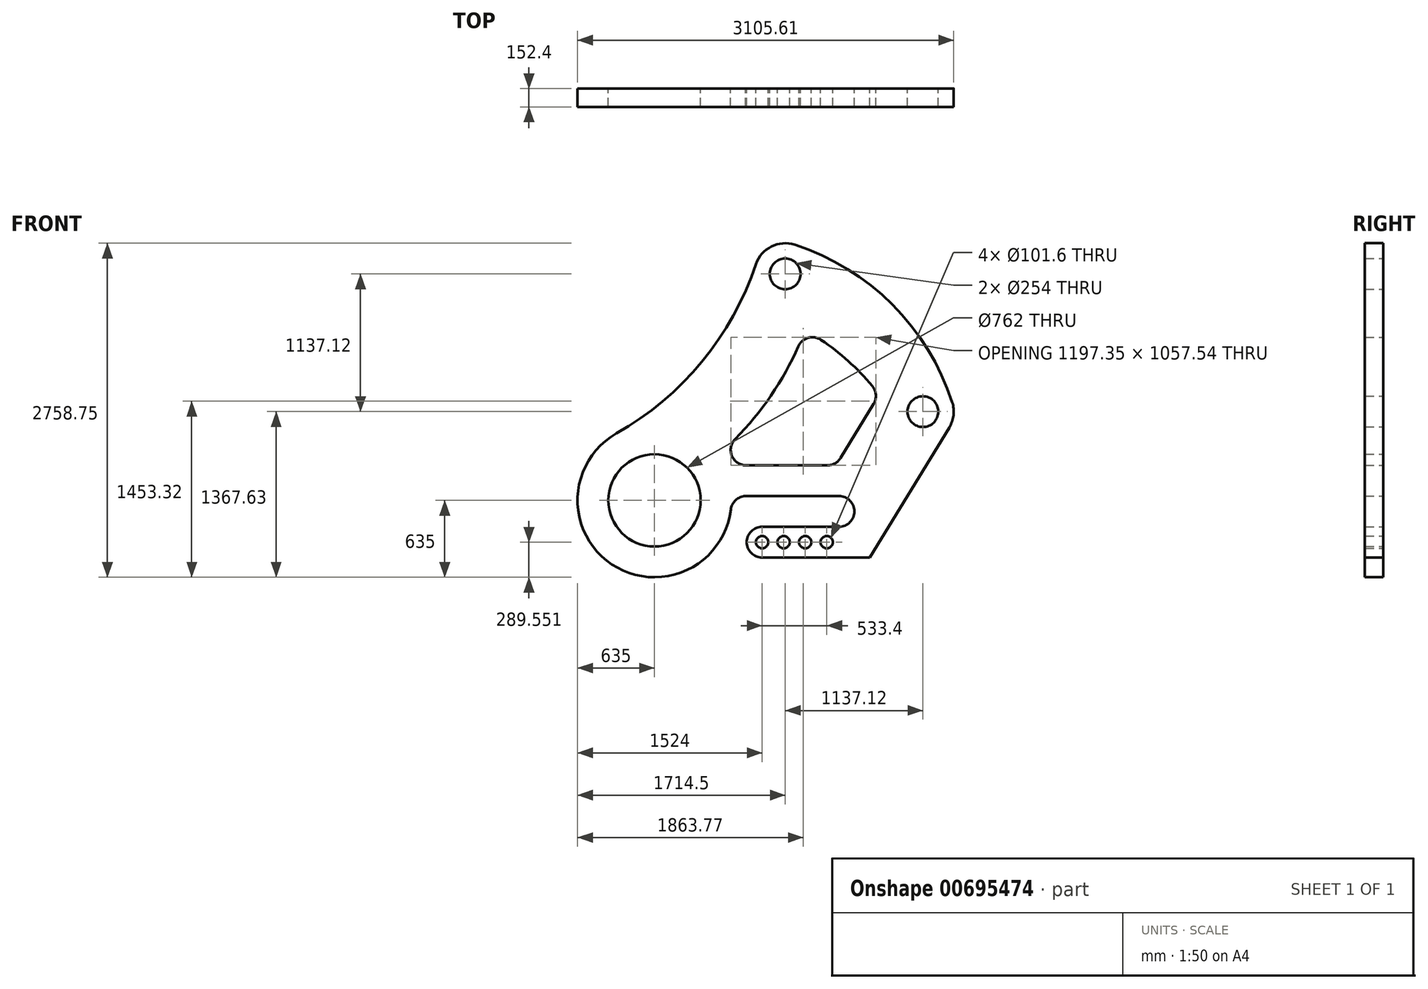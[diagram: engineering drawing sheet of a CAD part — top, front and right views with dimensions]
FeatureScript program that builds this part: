
annotation { "Feature Type Name" : "Feature", "Feature Type Description" : "" }
export const myFeature = defineFeature(function(context is Context, id is Id, definition is map)
    precondition{}
    {
        {
            var Q0;
            Q0=qCreatedBy(makeId("Front.planeOp"),FACE);
            var sketch = newSketch(context, id + "F0", { "sketchPlane" : qUnion([Q0])});
            skCircle(sketch, "E0", {"center": v(0, 0) * mm, "radius": 381 * mm});
            skLineSegment(sketch, "E1", {"start": v(-601.12, -1041.17) * mm, "end": v(1079.5, 1869.75) * mm, "construction": true});
            skArc(sketch, "E2", {"start": v(-313.75, 552.07) * mm, "mid": v(-351.76, -528.67) * mm, "end": v(630.42, -76.15) * mm});
            skCircle(sketch, "E3", {"center": v(1079.5, 1869.75) * mm, "radius": 127 * mm});
            skLineSegment(sketch, "E4", {"start": v(989.7, 1959.55) * mm, "end": v(2306.42, 642.83) * mm, "construction": true});
            skArc(sketch, "E5", {"start": v(1158.47, 2111.16) * mm, "mid": v(965.57, 2096.77) * mm, "end": v(838.75, 1950.71) * mm});
            skArc(sketch, "E6", {"start": v(-313.75, 552.07) * mm, "mid": v(391.49, 1145.1) * mm, "end": v(838.75, 1950.71) * mm});
            skLineSegment(sketch, "E7", {"start": v(889, -472.45) * mm, "end": v(1778, -472.45) * mm});
            skLineSegment(sketch, "E8", {"start": v(889, -218.45) * mm, "end": v(1524, -218.45) * mm});
            skPoint(sketch, "E9", {"position": v(889, -345.45) * mm});
            skArc(sketch, "E10", {"start": v(889, -218.45) * mm, "mid": v(762, -345.45) * mm, "end": v(889, -472.45) * mm});
            skArc(sketch, "E11", {"start": v(1524, -218.45) * mm, "mid": v(1651, -91.45) * mm, "end": v(1524, 35.55) * mm});
            skLineSegment(sketch, "E12", {"start": v(1778, -472.45) * mm, "end": v(2303.49, 971.32) * mm, "construction": true});
            skCircle(sketch, "E13", {"center": v(2216.61, 732.63) * mm, "radius": 127 * mm});
            skArc(sketch, "E14", {"start": v(2396.22, 553.03) * mm, "mid": v(2463.66, 673.58) * mm, "end": v(2458.03, 811.6) * mm});
            skLineSegment(sketch, "E15", {"start": v(1778, -472.45) * mm, "end": v(2433.36, 600.2) * mm});
            skArc(sketch, "E16", {"start": v(752.18, 35.55) * mm, "mid": v(670.65, 2.21) * mm, "end": v(630.42, -76.15) * mm});
            skLineSegment(sketch, "E17.trimOffspring", {"start": v(752.18, 35.55) * mm, "end": v(1524, 35.55) * mm});
            skArc(sketch, "E18", {"start": v(2458.03, 811.6) * mm, "mid": v(1963.57, 1616.7) * mm, "end": v(1158.47, 2111.16) * mm});
            skLineSegment(sketch, "E19.trimOffspring", {"start": v(2396.22, 553.03) * mm, "end": v(2401.38, 547.87) * mm, "construction": true});
            skLineSegment(sketch, "E20", {"start": v(756.5, 289.55) * mm, "end": v(1428.19, 289.55) * mm});
            skLineSegment(sketch, "E21", {"start": v(1809.16, 796.52) * mm, "end": v(1536.56, 350.34) * mm});
            skArc(sketch, "E22", {"start": v(1428.19, 289.55) * mm, "mid": v(1490.31, 305.78) * mm, "end": v(1536.56, 350.34) * mm});
            skArc(sketch, "E23", {"start": v(1809.16, 796.52) * mm, "mid": v(1827.44, 872.12) * mm, "end": v(1798.2, 944.2) * mm});
            skArc(sketch, "E24", {"start": v(666.96, 506.61) * mm, "mid": v(639.1, 368.12) * mm, "end": v(756.5, 289.55) * mm});
            skArc(sketch, "E25", {"start": v(1375.1, 1325.65) * mm, "mid": v(1268.83, 1342.34) * mm, "end": v(1187.88, 1271.5) * mm});
            skArc(sketch, "E26", {"start": v(665.73, 505.37) * mm, "mid": v(962.06, 864.41) * mm, "end": v(1187.88, 1271.5) * mm});
            skArc(sketch, "E27.trimOffspring", {"start": v(1798.2, 944.2) * mm, "mid": v(1600.09, 1149.83) * mm, "end": v(1375.1, 1325.65) * mm});
            skPoint(sketch, "E28.start.orphan", {"position": v(1912.72, 793.55) * mm});
            skPoint(sketch, "E29.orphan", {"position": v(1912.72, 966.01) * mm});
            skCircle(sketch, "E30", {"center": v(889, -345.45) * mm, "radius": 50.8 * mm});
            skCircle(sketch, "E31", {"center": v(1066.8, -345.45) * mm, "radius": 50.8 * mm});
            skCircle(sketch, "E32", {"center": v(1244.6, -345.45) * mm, "radius": 50.8 * mm});
            skCircle(sketch, "E33", {"center": v(1422.4, -345.45) * mm, "radius": 50.8 * mm});
            skSolve(sketch);
        }
        {
            var Q0;
            Q0=makeQuery(id+"F0.imprint","IMPRINT",FACE,{"disambiguationData":[TD([[makeQuery(id+"F0.imprint","IMPRINT",EDGE,{"derivedFrom":sQuery(id+"F0.wireOp",EDGE,"E0")}),-1.0]])]});
            extrude(context, id + "F1", {"entities" : qUnion([Q0]), "depth" : 152.4 * mm, "offsetDistance" : 25.4 * mm, "symmetric" : true});
        }
    });
